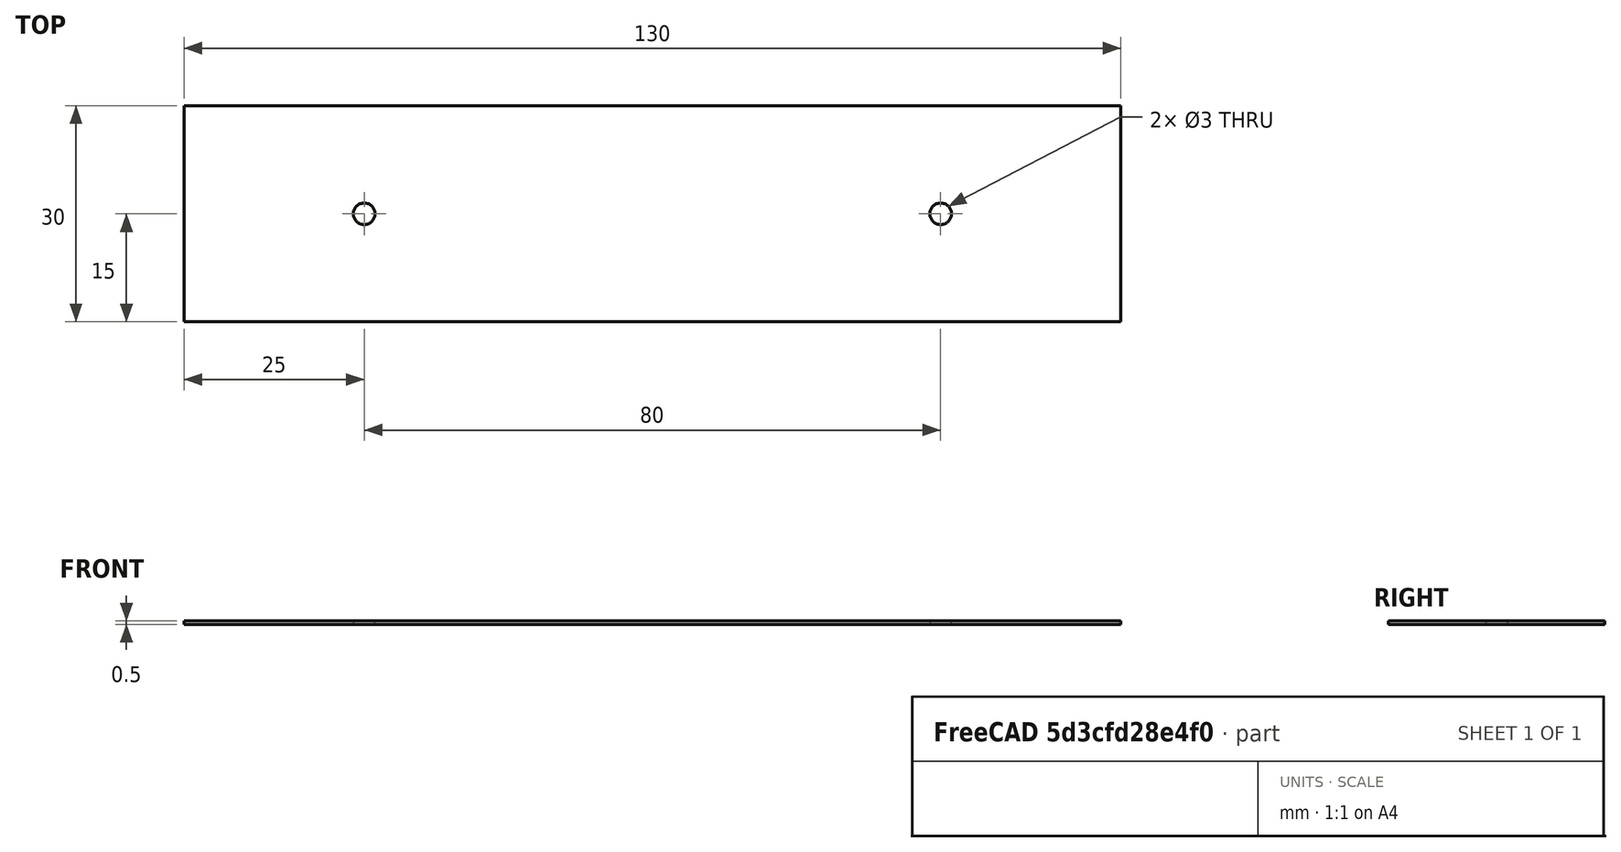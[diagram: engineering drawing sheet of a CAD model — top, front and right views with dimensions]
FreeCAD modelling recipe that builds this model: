
FCSTD DOCUMENT  (FreeCAD 0.19R24276 (Git))
Label: plate_130x30xh0_5
License: All rights reserved
LicenseURL: http://en.wikipedia.org/wiki/All_rights_reserved
objects: Sketcher::SketchObject×1, PartDesign::Pad×1, PartDesign::Body×1
note: 4 computed .brp shape members not serialized (recipe doc carries the construction recipe); baked Part::Feature solids carry a one-line shape summary decoded from their .brp

FEATURE [Sketcher::SketchObject] Sketch
  FullyConstrained = true
  MapMode = 5
  Support = -> [XY_Plane]
  sketch-geometry (7):
    g0: LineSegment StartX=0 StartY=0 StartZ=0 EndX=130 EndY=0 EndZ=0
    g1: LineSegment StartX=130 StartY=0 StartZ=0 EndX=130 EndY=30 EndZ=0
    g2: LineSegment StartX=130 StartY=30 StartZ=0 EndX=0 EndY=30 EndZ=0
    g3: LineSegment StartX=0 StartY=30 StartZ=0 EndX=0 EndY=0 EndZ=0
    g4: Circle CenterX=25 CenterY=15 CenterZ=0 NormalX=0 NormalY=0 NormalZ=1 AngleXU=0 Radius=1.5
    g5: Circle CenterX=105 CenterY=15 CenterZ=0 NormalX=0 NormalY=0 NormalZ=1 AngleXU=0 Radius=1.5
    g6: LineSegment StartX=25 StartY=15 StartZ=0 EndX=105 EndY=15 EndZ=0
  constraints (19):
    c: Coincident(g0,g1)
    c: Coincident(g1,g2)
    c: Coincident(g2,g3)
    c: Coincident(g3,g0)
    c: Horizontal(g0)
    c: Horizontal(g2)
    c: Vertical(g1)
    c: Vertical(g3)
    c: Coincident(g0,g-1)
    c: DistanceX(g0,g0) = 130
    c: DistanceY(g3,g3) = 30
    c: Coincident(g6,g4)
    c: Coincident(g6,g5)
    c: Horizontal(g6)
    c: Diameter(g4) = 3
    c: Equal(g4,g5)
    c: DistanceX(g0,g4) = 25
    c: DistanceX(g5,g1) = 25
    c: DistanceY(g0,g4) = 15
FEATURE [PartDesign::Pad] Pad  label="Pad_h0,5"
  Direction = (1,1,1)
  Length = 0.5
  Length2 = 100
  Profile = -> Sketch
  Type = 0
FEATURE [PartDesign::Body] Body
  Group = -> [Sketch,Pad]
  Origin = -> Origin
  Tip = -> Pad
